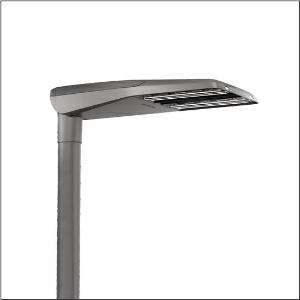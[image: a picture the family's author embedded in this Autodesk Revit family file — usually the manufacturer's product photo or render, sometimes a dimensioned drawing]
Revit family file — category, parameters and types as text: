
# Revit family: streetlight_sl_11_iq_midi___st1_2a_5xc3a31f08me_35e9
name_source: partatom
category: Lighting Fixtures
units: mm (PartAtom-declared; Revit-internal decimal feet)

## family parameters
Cut with Voids When Loaded = No
Host = Face
Light Source = No
Part Type = Normal
Room Calculation Point = No
Round Connector Dimension = Use Diameter
Shared = No

## types (1)
- --- (1 x LED, 15580 lm, 124.7 W, 3000K)
    Apparent Load = 125 VA
    CIE Flux Codes = 32 70 96 100 100
    Color Rendering = 80
    Color Temperature = 3000K
    Default Elevation = 1800 mm
    Description = Streetlight SL 11 iQ midi, mast luminaire, primary light control with 3 zone facetted reflector, of plastic, silver coated, highly specular, primary optical cover: cover, of PMMA, transparent, light distribution: ST1.2a, light emission: direct distribution, primary light characteristic: asymmetric, installation type: post-top, side-entry, LED, High Power LED, rated luminous flux: 15.580lm, luminous efficacy: 125lm/W, light colour: 830, colour temperature: 3000K, control: Street-Remote, optimised constant luminous flux control (CLO 2.0), Desk-Remote (wireless, voltage-free reading and setting of iQ features in the workshop via application-optimized NFC function/RFID function), Light-Fading, Smart-Wire, Night-Set, Lumen-Switch, Temp-Guard, Auto-Match, with cable H07RN-F 5x 1.5mm², mains connection: 230..240V, AC, 50/60Hz, connection cable pre-assembled, cable length: 12,5m, start of lifetime: 125W, end of service life: 132W, reduction: 57W, luminaire housing, of diecast aluminium, powder-coated, Siteco® metallic grey (DB 702S), please order mast flange separately, inclination adjustable without tools: 0°, 5°, 10°, 15° (post-top) | 0°, -5°, -10°, -15° (side-entry), sealing non-destructively replaceable, multi-level sealing system, length: 780mm, width: 376mm, height: 118mm, mast flange for spigot size: 42mm (side-entry): 5XC10008XM4, 60/48mm (side-entry/post-top): 5XC10108XM2, 76/60mm (side-entry/post-top): 5XC10108XM1, equipment: Power, protection rating (complete): IP66, insulation class (complete): insulation class II (safety insulation), certification: CE, ENEC, VDE, impact resistance: IK09, permissible operating ambient temperature for outdoor applications: -25..+50°C, standard-compliant lighting for roads and squares, Environmental Product Declaration (EPD) tested and certified by an independent institute, packaging unit: 1 piece

Light Distribution: ST1.2a
    Height = 118 mm
    Lamp = 1 x LED
    Lamp Light Flux = 15580 lm
    Lamp Power = 124.7 W
    Lamp count = 1
    Length = 780 mm
    Luminous efficacy = 125 lm/W
    Manufacturer = Siteco
    ModVariant = No
    Model = 5XC3A31F08ME
    Number of Poles = 1
    OnlyDefault = Yes
    Power Factor = 1
    Product Name = Streetlight SL 11 iQ midi | ST1.2a
    Product group = mast luminaire | pylon top
    ProductGroupID = 6100
    Protection Class = Protection class II
    Protection Degree = IP 66
    RLX_Detail_Level = 1
    RLX_Emergency_Light_Flux = 0 lm
    RLX_Emergency_Type = 0
    RLX_Emergency_Type_DB = No
    RlxData = <blob elided: 70689 chars, md5=17e9203e>
    Socket = socket
    Standby Power = 0 W
    System Light Flux = 15580 lm
    System Power = 125 W
    Type Comments = factory setting: luminous flux: 100 % | dim-lin: 254 | 557 mA
    Type Image = l_1005960.jpg
    URL = http://relux.com
    VarID = @adj_131661
    Voltage = 0 V
    Weight = 0.00 kg
    Width = 376 mm

## geometry (parser evidence)
native form markers: Blend x4, Sweep x10
no freeform markers — native parametric forms only
